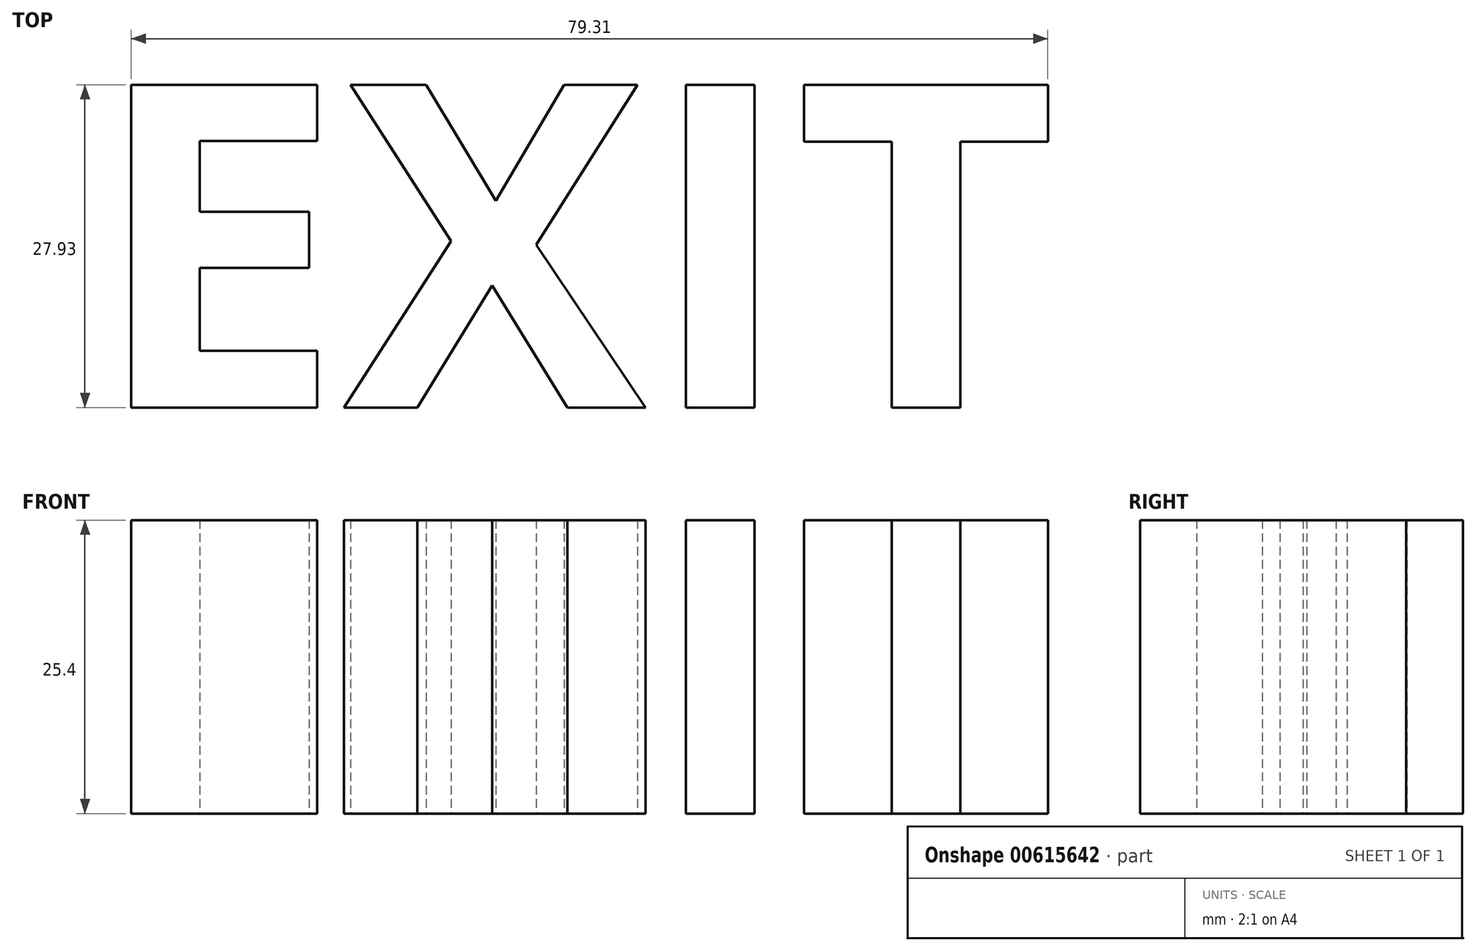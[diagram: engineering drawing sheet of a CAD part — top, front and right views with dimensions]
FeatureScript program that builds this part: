
annotation { "Feature Type Name" : "Feature", "Feature Type Description" : "" }
export const myFeature = defineFeature(function(context is Context, id is Id, definition is map)
    precondition{}
    {
        {
            var Q0;
            Q0=qCreatedBy(makeId("Top.planeOp"),FACE);
            var sketch = newSketch(context, id + "F0", { "sketchPlane" : qUnion([Q0])});
            skText(sketch, "E0", { "text": "EXIT", "fontName": "OpenSans-Bold.ttf"});
            const initialGuessF0  = {"E0": [-0.04429, 0.00436, 1, 0, 0.02817]};
            skSetInitialGuess(sketch, initialGuessF0);
            skSolve(sketch);
        }
        {
            var Q0;
            Q0 = qSketchRegion(id + "F0", true);
            extrude(context, id + "F1", {"entities" : qUnion([Q0]), "depth" : 25.4 * mm, "offsetDistance" : 25.4 * mm});
        }
    });
